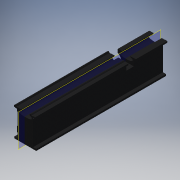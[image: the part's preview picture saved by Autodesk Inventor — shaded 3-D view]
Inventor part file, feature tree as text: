
AUTODESK INVENTOR PART (.ipt)
format: ipt  version: 2016 (Build 200138000, 138)  size: 387,072 bytes
history: native  units: in
note: dims shown in document units (in); Inventor stores cm internally (conversion verified against a paired STEP export)
features: extrude x10, sketch x10, plane x3, chamfer x1
ambient origin geometry x8: Origin, YZ Plane, XZ Plane, XY Plane, X Axis, Y Axis, Z Axis, Center Point
bodies: Solid1 (feature_tree)
feature tree (24):
  extrude  "Extrusion1"  TaperAngle=150.0deg  [1 undecoded]
  chamfer  "Chamfer1"  Distance=0.0787in
  plane  "Work Plane3"
  extrude  "Extrusion2"  Depth=0.0787in
  extrude  "Extrusion3"  Depth=0.0787in
  extrude  "Extrusion4"  Depth=0.0787in
  extrude  "Extrusion5"  Depth=0.0787in
  extrude  "Extrusion6"  TaperAngle=120.0deg  [1 undecoded]
  extrude  "Extrusion7"  Depth=0.1575in
  extrude  "Extrusion8"  Depth=0.0787in
  plane  "Work Plane4"
  plane  "Work Plane5"
  extrude  "Extrusion9"  Depth=0.0787in
  extrude  "Extrusion10"  Depth=0.0787in
  sketch  "Sketch1"  dims[d0=0.4331in d1=150.0deg]
  sketch  "Sketch2"  dims[d2=0.3937in]
  sketch  "Sketch3"  dims[d3=0.4606in]
  sketch  "Sketch4"  dims[d4=0.4961in]
  sketch  "Sketch5"  dims[d5=0.962in]
  sketch  "Sketch6"  dims[d6=0.1496in]
  sketch  "Sketch8"  dims[d7=0.4016in]
  sketch  "Sketch9"  dims[d8=0.962in]
  sketch  "Sketch10"  dims[d9=0.126in]
  sketch  "Sketch11"  dims[d10=0.6339in d11=0.0787in d12=0.9921in d13=0.6181in d14=0.5787in d15=0.315in d16=120.0deg d17=0.1575in d18=2.4409in d19=8.0315in d22=3.6299in d24=0.5in d25=1.4252in d26=180.0deg d27=0.0787in d28=0.748in d29=0.0787in d30=0.5197in d31=0.962in d32=0.1811in d33=0.6299in d34=0.962in d35=0.5512in d36=0.5512in d37=90.0deg d38=0.1181in d39=60.0deg d40=0.685in d41=0.8858in d43=5.2953in d44=90.0deg d46=2.185in d47=90.0deg d50=90.0deg d51=1.378in d52=180.0deg d53=0.7087in d54=90.0deg d55=1.378in d57=0.7087in d59=180.0deg d60=0.315in d61=120.0deg d62=2.4409in d63=55.9055in d64=0.0in d65=0.1575in d66=0.0787in d67=45.0deg d68=40.1575in d69=3.2283in d70=3.4528in d71=55.9055in d72=0.0in d73=55.9055in d74=0.0in d75=55.9055in d76=0.0in d77=3.3465in d78=1.2205in d79=1.7323in d80=55.9055in d81=0.0in d82=1.0236in d83=0.0in d84=0.315in d85=0.315in d86=0.7283in d87=0.5512in d88=0.5118in d89=0.3937in d90=0.0in d91=0.315in d92=0.315in d93=6.7717in d94=0.8858in d95=0.5512in d96=0.7874in d97=0.0in d98=0.2756in d99=0.3937in d100=0.0in d101=5.5118in d102=1.9685in d103=0.2756in d104=1.5748in d105=0.0787in d106=0.0in]
note: 2 required parameter values undecoded (feature->parameter linkage not recoverable at this tier; creation-order binding heuristic only, values carry confidence <= 0.55)
